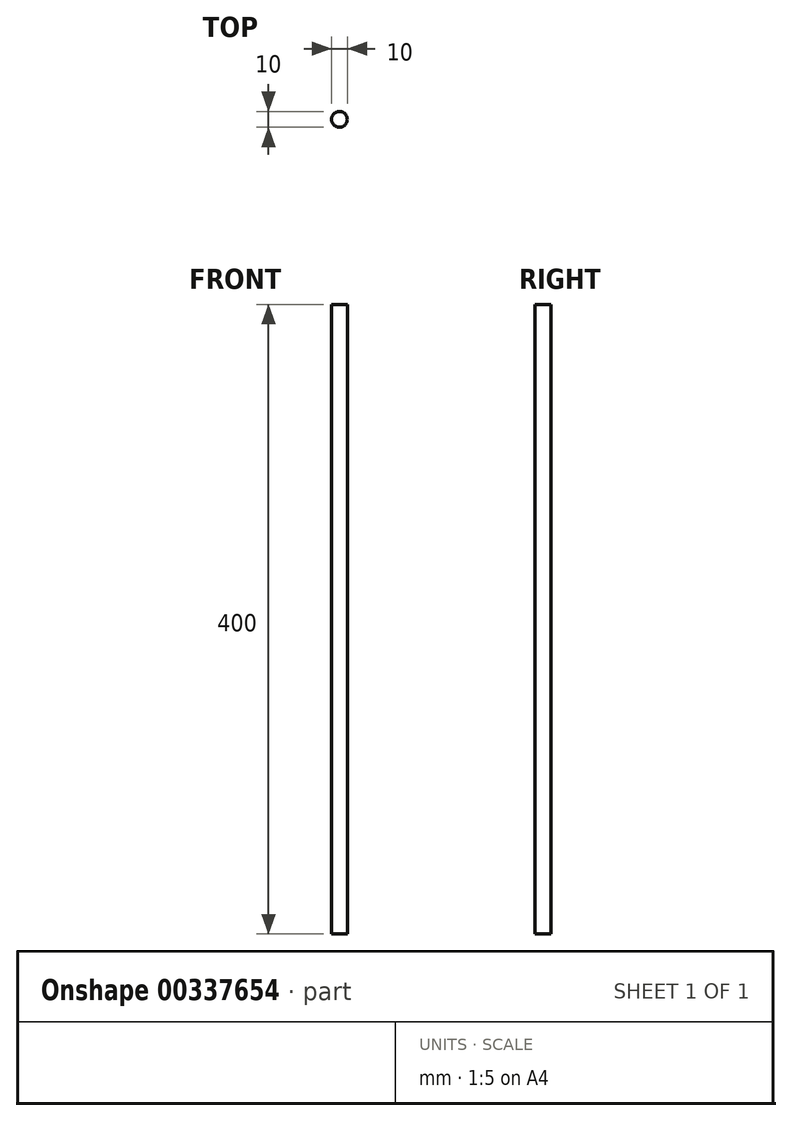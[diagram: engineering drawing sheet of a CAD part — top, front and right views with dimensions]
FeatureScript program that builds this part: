
annotation { "Feature Type Name" : "Feature", "Feature Type Description" : "" }
export const myFeature = defineFeature(function(context is Context, id is Id, definition is map)
    precondition{}
    {
        {
            var Q0;
            Q0=qCreatedBy(makeId("Top.planeOp"),FACE);
            var sketch = newSketch(context, id + "F0", { "sketchPlane" : qUnion([Q0])});
            skCircle(sketch, "E0", {"center": v(0, 0) * mm, "radius": 5 * mm});
            skSolve(sketch);
        }
        {
            var Q0;
            Q0=makeQuery(id+"F0.imprint","IMPRINT",FACE,{"disambiguationData":[TD([[makeQuery(id+"F0.imprint","IMPRINT",EDGE,{"derivedFrom":sQuery(id+"F0.wireOp",EDGE,"E0")}),1.0]])]});
            extrude(context, id + "F1", {"entities" : qUnion([Q0]), "oppositeDirection" : true, "depth" : 200 * mm, "hasSecondDirection" : true, "secondDirectionOppositeDirection" : false, "secondDirectionDepth" : 200 * mm});
        }
    });
